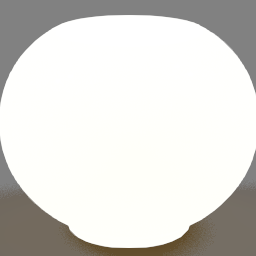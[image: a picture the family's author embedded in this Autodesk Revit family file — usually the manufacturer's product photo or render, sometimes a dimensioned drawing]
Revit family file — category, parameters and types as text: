
# Revit family: 3-080X-xx Dusk Mirror
name_source: partatom
category: Luminarias
units: mm (PartAtom-declared; Revit-internal decimal feet)

## family parameters
Anfitrión = Muro
Compartido = No
Corte con vacíos al cargar = No
Cota de conector redondo = Diámetro de uso
Número OmniClass = 23.80.70.00
Origen de luz = No
Punto de cálculo de habitación = No
Siempre vertical = Sí
Tipo de pieza = Normal
Título OmniClass = Lighting

## types (4) — shared parameters
Diffuser = Ghost Mirror
Fabricante = Vanita by Oxygen
Lámpara = LED Array
Metal Finish 1 = 15 - Black
Modelo = 3-080X-xx / Dusk
References = Ref. 3 = 120 V / Ref. 37 = 277 V
URL = www.oxygenlighting.com
Voltage = 120 V
Voltage Input = 120 V or 277 V - 50/60 Hz
zero-valued in all types: Elevación por defecto

## per-type parameters (varying)
| type | Comentarios de vataje | Height | Width |
| 3-0801-15 / Black | 1 x 32.8 W at 120 V | 457 mm  [stored 1.49934 ft] | 610 mm  [stored 2.00131 ft] |
| 3-0803-15 / Black | 1 x 66.9 W at 120 V | 914 mm  [stored 2.99869 ft] | 914 mm  [stored 2.99869 ft] |
| 3-0804-15 / Black | 1 x 87.7 W at 120 V | 914 mm  [stored 2.99869 ft] | 1219 mm |
| 3-0802-15 / Black | 1 x 60.9 W at 120 V | 914 mm  [stored 2.99869 ft] | 610 mm  [stored 2.00131 ft] |

note: [stored X ft] marks values corroborated as IEEE doubles in the binary element streams (Revit-internal decimal feet)

## geometry (parser evidence)
native form markers: Sweep x5
no freeform markers — native parametric forms only
